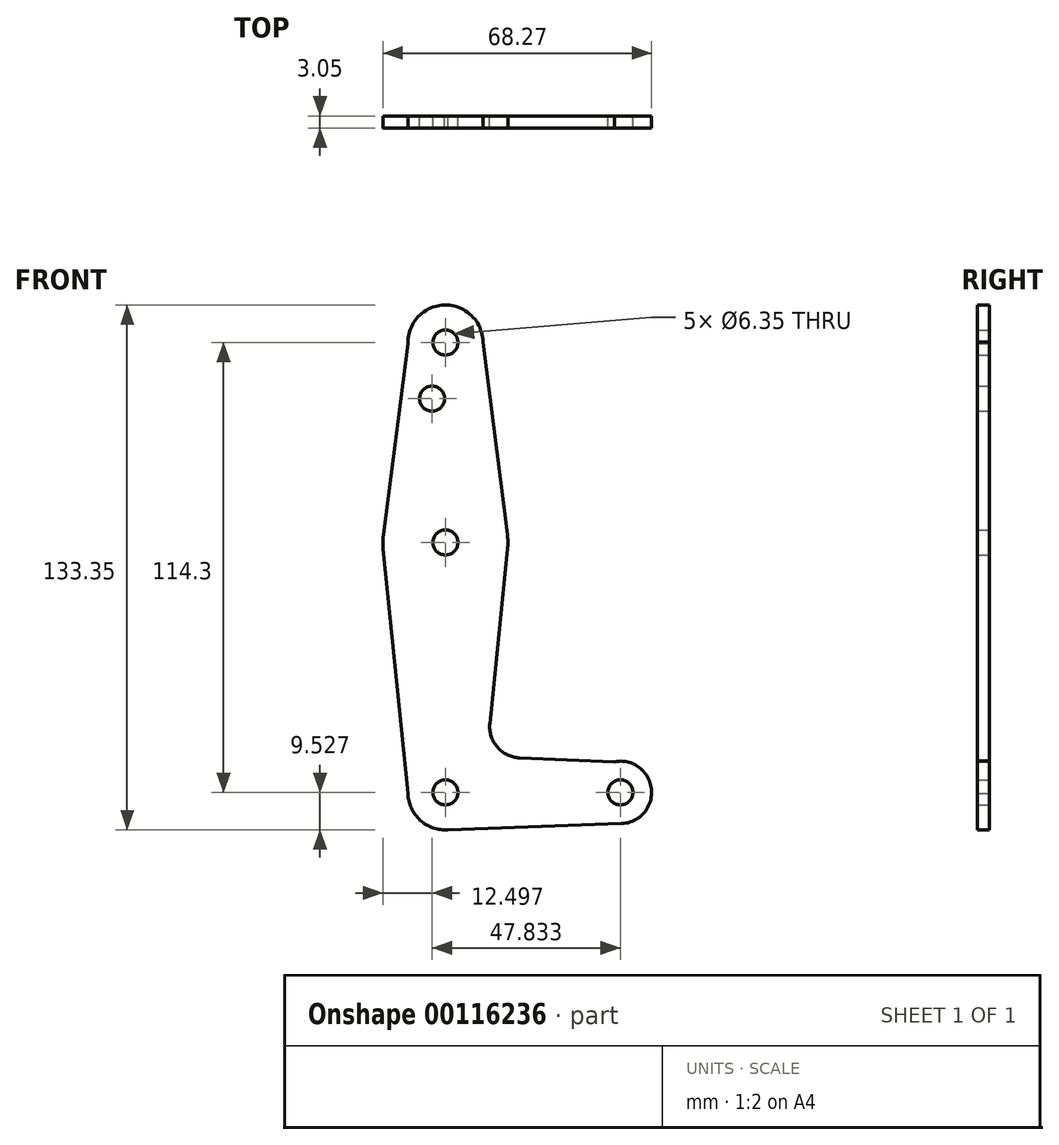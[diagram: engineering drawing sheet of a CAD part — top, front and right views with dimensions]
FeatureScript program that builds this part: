
annotation { "Feature Type Name" : "Feature", "Feature Type Description" : "" }
export const myFeature = defineFeature(function(context is Context, id is Id, definition is map)
    precondition{}
    {
        {
            var Q0;
            Q0=qCreatedBy(makeId("Front.planeOp"),FACE);
            var sketch = newSketch(context, id + "F0", { "sketchPlane" : qUnion([Q0])});
            skLineSegment(sketch, "E0", {"start": v(0, 56.53) * mm, "end": v(0, -57.77) * mm});
            skLineSegment(sketch, "E1", {"start": v(0, -57.77) * mm, "end": v(0, 5.73) * mm, "construction": true});
            skCircle(sketch, "E2", {"center": v(0, 5.73) * mm, "radius": 15.88 * mm});
            skCircle(sketch, "E3", {"center": v(0, 56.53) * mm, "radius": 9.53 * mm});
            skCircle(sketch, "E4", {"center": v(0, -57.77) * mm, "radius": 9.53 * mm});
            skLineSegment(sketch, "E5", {"start": v(0, -57.77) * mm, "end": v(44.45, -57.77) * mm});
            skCircle(sketch, "E6", {"center": v(44.45, -57.77) * mm, "radius": 7.94 * mm});
            skLineSegment(sketch, "E7", {"start": v(-9.52, 56.22) * mm, "end": v(-15.75, 7.75) * mm});
            skLineSegment(sketch, "E8", {"start": v(-9.52, -58.05) * mm, "end": v(-15.8, 4.13) * mm});
            skLineSegment(sketch, "E9", {"start": v(9.52, 56.63) * mm, "end": v(15.75, 7.73) * mm});
            skLineSegment(sketch, "E10", {"start": v(11.27, -40.25) * mm, "end": v(15.8, 4.12) * mm});
            skLineSegment(sketch, "E11", {"start": v(42.97, -49.97) * mm, "end": v(18.86, -49) * mm});
            skLineSegment(sketch, "E12", {"start": v(0, -67.3) * mm, "end": v(44.73, -65.7) * mm});
            skArc(sketch, "E13.filletArc", {"start": v(11.27, -40.25) * mm, "mid": v(13.18, -46.27) * mm, "end": v(18.86, -49) * mm});
            skCircle(sketch, "E14", {"center": v(44.45, -57.77) * mm, "radius": 3.18 * mm});
            skCircle(sketch, "E15", {"center": v(0, -57.77) * mm, "radius": 3.18 * mm});
            skCircle(sketch, "E16", {"center": v(0, 5.73) * mm, "radius": 3.18 * mm});
            skCircle(sketch, "E17", {"center": v(0, 56.53) * mm, "radius": 3.18 * mm});
            skLineSegment(sketch, "E18", {"start": v(0, 5.73) * mm, "end": v(0, 42.25) * mm});
            skCircle(sketch, "E19", {"center": v(-3.38, 42.25) * mm, "radius": 3.18 * mm});
            skSolve(sketch);
        }
        {
            var Q0;
            Q0 = qSketchRegion(id + "F0", true);
            var Q1;
            {var subQ0=sQuery(id+"F0.wireOp",EDGE,"E4");var subQ1=sQuery(id+"F0.wireOp",EDGE,"E0");var subQ2=makeQuery(id+"F0.imprint","INTERSECT",VERTEX,{"derivedFrom":[subQ1,subQ0]});Q1=makeQuery(id+"F0.imprint","IMPRINT",FACE,{"disambiguationData":[TD([[makeQuery(id+"F0.imprint","IMPRINT",EDGE,{"disambiguationData":[TD([[subQ2,-1.0]])],"derivedFrom":subQ1}),1.0]])]});}
            extrude(context, id + "F1", {"entities" : qUnion([Q0, Q1]), "depth" : 3.05 * mm});
        }
    });
